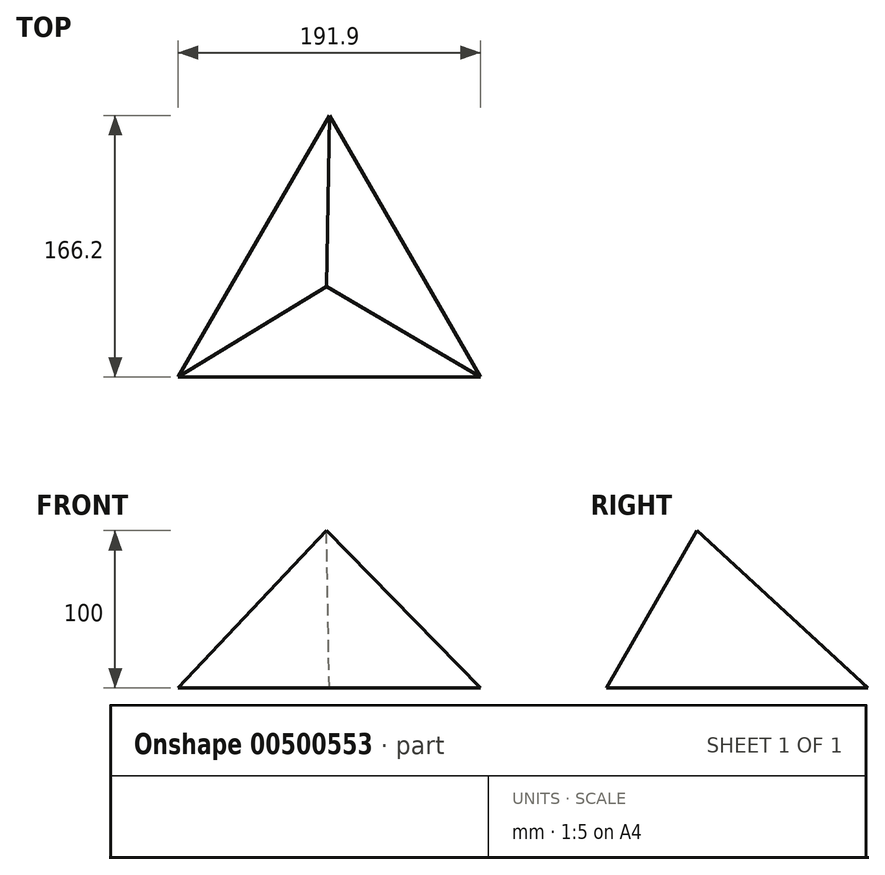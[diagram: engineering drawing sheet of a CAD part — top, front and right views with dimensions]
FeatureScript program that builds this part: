
annotation { "Feature Type Name" : "Feature", "Feature Type Description" : "" }
export const myFeature = defineFeature(function(context is Context, id is Id, definition is map)
    precondition{}
    {
        {
            var Q0;
            Q0=qCreatedBy(makeId("Top.planeOp"),FACE);
            var sketch = newSketch(context, id + "F0", { "sketchPlane" : qUnion([Q0])});
            skCircle(sketch, "E0.cCircle", {"center": v(0, 0) * mm, "radius": 110.8 * mm, "construction": true});
            skLineSegment(sketch, "E0.0", {"start": v(0, 110.8) * mm, "end": v(95.95, -55.4) * mm});
            skLineSegment(sketch, "E0.1", {"start": v(95.95, -55.4) * mm, "end": v(-95.95, -55.4) * mm});
            skLineSegment(sketch, "E0.2", {"start": v(-95.95, -55.4) * mm, "end": v(0, 110.8) * mm});
            skSolve(sketch);
        }
        {
            var Q0;
            Q0=qCreatedBy(makeId("Top.planeOp"),FACE);
            cPlane(context, id + "F1", {"entities" : qUnion([Q0]), "cplaneType" : CPlaneType.OFFSET, "offset" : 100 * mm, "width" : 152.4 * mm, "height" : 152.4 * mm});
        }
        {
            var Q0;
            Q0=qCreatedBy(id+"F1.planeOp",FACE);
            var sketch = newSketch(context, id + "F2", { "sketchPlane" : qUnion([Q0])});
            skPoint(sketch, "E1", {"position": v(-1.75, 2.19) * mm});
            skSolve(sketch);
        }
        {
            var Q0;
            Q0=makeQuery(id+"F0.imprint","IMPRINT",FACE,{"disambiguationData":[TD([[makeQuery(id+"F0.imprint","IMPRINT",EDGE,{"derivedFrom":sQuery(id+"F0.wireOp",EDGE,"E0.0")}),-1.0]])]});
            var Q1;
            Q1=sQuery(id+"F2.wireOp",VERTEX,"E1");
            loft(context, id + "F3", {"sheetProfilesArray" : [{ "sheetProfileEntities" : qUnion([Q0]) }, { "sheetProfileEntities" : qUnion([Q1]) }]});
        }
    });
